# Revit family: 3L-WS-D
name_source: partatom
category: Lighting Fixtures
units: mm (PartAtom-declared; Revit-internal decimal feet)

## family parameters
Cut with Voids When Loaded = No
Host = Face
Light Source = Yes
OmniClass Number = 23.80.70.11.14.17
OmniClass Title = Direct/Indirect
Part Type = Normal
Room Calculation Point = No
Round Connector Dimension = Use Diameter
Shared = Yes

## types (2) — shared parameters
Apparent Load = 0 VA
Application = Commercial Indoor,Institutional,Retail,Education,Healthcare,Library,Office,Perimeter Lighting,Public Space
Assembly Code = D5020200
Bulb = Glass -  White
Circuiting = 1Circuit
Color Filter = 16777215
Default Elevation = 48 "
Depth = 4.313 "
Description = MOD™ 3 LED Perimeter Wall/Slot® Direct
Dimming Lamp Color Temperature Shift = <None>
Emit Shape Visible in Rendering = No
Emit from Rectangle Length = 3.5 "
Emit from Rectangle Width = 47 "
Ending Length = 24 "
Features = Variable Intensity technology provides specifiable
lumen output/wattage
• End cap design eliminates visible diffuser seams/gaps
• 2 SDCM color variation
Fixture Distribution = Direct/Asymmetric Direct
Glass = Paint -Textured Matte White
Height = 10.5 "
Housing Material = Paint - Matte White
Lamp = LED
Load Classification = Lighting
Manufacturer = Litecontrol
Model = MOD™ 3 LED Perimeter Wall/Slot® Direct
Mounting = Perimeter
Photometric Notes = More IES files download on Photometric Link
Power Factor = 1
Row Length = 48 "
Starting Length = -24 "
Tilt Angle = 90.00°
Type Comments = Lighting Fixture
URL = https://www.currentlighting.com
Voltage = 120 V
Warranty = 5-Years Warranty
Wattage Comments = 18W
Width = 3.5 "

## per-type parameters (varying)
| type | Photometric Web File |
| 3L-WS-D-4-NRW | 3L-WSx-D-4-NRW-X-CX-35K-D035.ies |
| 3L-WS-D-4-SOF | 3L-WSx-D-4-SOF-X-CX-35K-D035.ies |

## geometry (parser evidence)
native form markers: Sweep x2
no freeform markers — native parametric forms only
